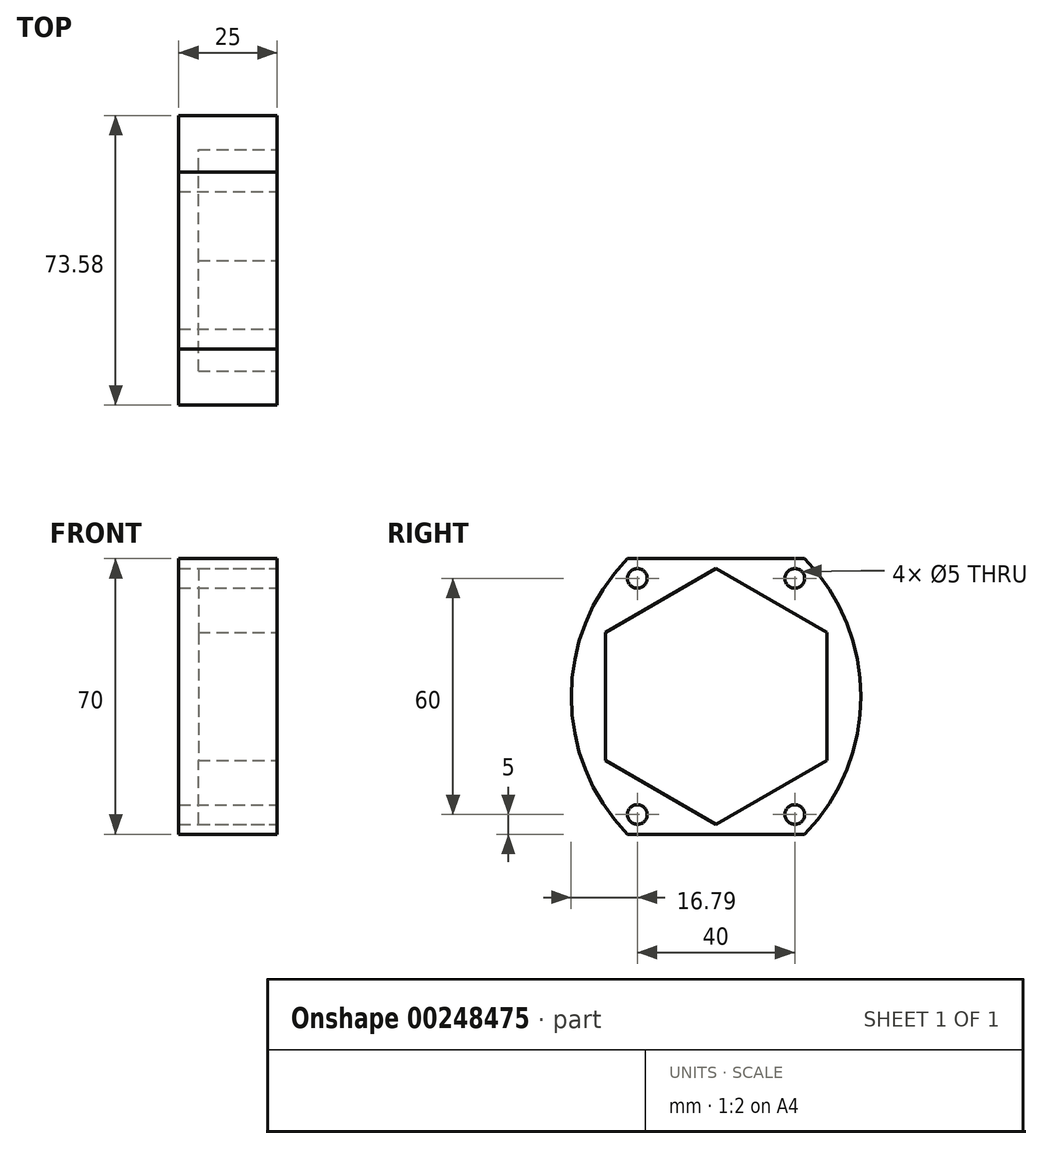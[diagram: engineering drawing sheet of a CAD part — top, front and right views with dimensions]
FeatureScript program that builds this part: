
annotation { "Feature Type Name" : "Feature", "Feature Type Description" : "" }
export const myFeature = defineFeature(function(context is Context, id is Id, definition is map)
    precondition{}
    {
        {
            var Q0;
            Q0=qCreatedBy(makeId("Right.planeOp"),FACE);
            var sketch = newSketch(context, id + "F0", { "sketchPlane" : qUnion([Q0])});
            skArc(sketch, "E0", {"start": v(22.5, -35) * mm, "mid": v(36.8, 0) * mm, "end": v(22.5, 35) * mm});
            skLineSegment(sketch, "E1", {"start": v(22.5, 35) * mm, "end": v(-22.5, 35) * mm});
            skLineSegment(sketch, "E2", {"start": v(22.5, -35) * mm, "end": v(-22.5, -35) * mm});
            skLineSegment(sketch, "E3", {"start": v(22.5, 35) * mm, "end": v(22.5, -35) * mm, "construction": true});
            skLineSegment(sketch, "E4", {"start": v(-22.5, 35) * mm, "end": v(-22.5, -35) * mm, "construction": true});
            skArc(sketch, "E5", {"start": v(-22.5, 35) * mm, "mid": v(-36.8, 0) * mm, "end": v(-22.5, -35) * mm});
            skLineSegment(sketch, "E6", {"start": v(-22.5, 0) * mm, "end": v(0, 0) * mm, "construction": true});
            skLineSegment(sketch, "E7", {"start": v(0, 0) * mm, "end": v(22.5, 0) * mm, "construction": true});
            skLineSegment(sketch, "E8", {"start": v(0, 35) * mm, "end": v(0, 0) * mm, "construction": true});
            skLineSegment(sketch, "E9", {"start": v(0, 0) * mm, "end": v(0, -35) * mm, "construction": true});
            skSolve(sketch);
        }
        {
            var Q0;
            Q0 = qSketchRegion(id + "F0", true);
            extrude(context, id + "F1", {"entities" : qUnion([Q0]), "depth" : 25 * mm});
        }
        {
            var Q0;
            Q0=makeQuery(id+"F1.opExtrude","CAP_FACE",FACE,{"disambiguationData":[OSD([sQuery(id+"F0.wireOp",EDGE,"E0"),sQuery(id+"F0.wireOp",EDGE,"E1"),sQuery(id+"F0.wireOp",EDGE,"E2"),sQuery(id+"F0.wireOp",EDGE,"E5")])],"isStart":false});
            var sketch = newSketch(context, id + "F2", { "sketchPlane" : qUnion([Q0])});
            skCircle(sketch, "E10.cCircle", {"center": v(0, 0) * mm, "radius": 32.5 * mm, "construction": true});
            skLineSegment(sketch, "E10.0", {"start": v(28.15, 16.25) * mm, "end": v(28.15, -16.25) * mm});
            skLineSegment(sketch, "E10.1", {"start": v(28.15, -16.25) * mm, "end": v(0, -32.5) * mm});
            skLineSegment(sketch, "E10.2", {"start": v(0, -32.5) * mm, "end": v(-28.15, -16.25) * mm});
            skLineSegment(sketch, "E10.3", {"start": v(-28.15, -16.25) * mm, "end": v(-28.15, 16.25) * mm});
            skLineSegment(sketch, "E10.4", {"start": v(-28.15, 16.25) * mm, "end": v(0, 32.5) * mm});
            skLineSegment(sketch, "E10.5", {"start": v(0, 32.5) * mm, "end": v(28.15, 16.25) * mm});
            skSolve(sketch);
        }
        {
            var Q0;
            Q0 = qSketchRegion(id + "F2", true);
            extrude(context, id + "F3", {"entities" : qUnion([Q0]), "operationType" : NewBodyOperationType.REMOVE, "oppositeDirection" : true, "depth" : 20 * mm});
        }
        {
            var Q0;
            Q0=makeQuery(id+"F1.opExtrude","CAP_FACE",FACE,{"disambiguationData":[OSD([sQuery(id+"F0.wireOp",EDGE,"E0"),sQuery(id+"F0.wireOp",EDGE,"E1"),sQuery(id+"F0.wireOp",EDGE,"E2"),sQuery(id+"F0.wireOp",EDGE,"E5")])],"isStart":false});
            var sketch = newSketch(context, id + "F4", { "sketchPlane" : qUnion([Q0])});
            skCircle(sketch, "E11", {"center": v(-20, 30) * mm, "radius": 2.5 * mm});
            skCircle(sketch, "E12", {"center": v(20, 30) * mm, "radius": 2.5 * mm});
            skCircle(sketch, "E13", {"center": v(20, -30) * mm, "radius": 2.5 * mm});
            skCircle(sketch, "E14", {"center": v(-20, -30) * mm, "radius": 2.5 * mm});
            skLineSegment(sketch, "E15", {"start": v(-20, 30) * mm, "end": v(0, 30) * mm, "construction": true});
            skLineSegment(sketch, "E16", {"start": v(0, 30) * mm, "end": v(20, 30) * mm, "construction": true});
            skLineSegment(sketch, "E17", {"start": v(-20, 30) * mm, "end": v(-20, 0) * mm, "construction": true});
            skLineSegment(sketch, "E18", {"start": v(-20, 0) * mm, "end": v(-20, -30) * mm, "construction": true});
            skLineSegment(sketch, "E19", {"start": v(20, 30) * mm, "end": v(20, 0) * mm, "construction": true});
            skLineSegment(sketch, "E20", {"start": v(20, 0) * mm, "end": v(20, -30) * mm, "construction": true});
            skSolve(sketch);
        }
        {
            var Q0;
            Q0 = qSketchRegion(id + "F4", true);
            extrude(context, id + "F5", {"entities" : qUnion([Q0]), "operationType" : NewBodyOperationType.REMOVE, "endBound" : BoundingType.THROUGH_ALL, "oppositeDirection" : true, "depth" : 25 * mm});
        }
    });
